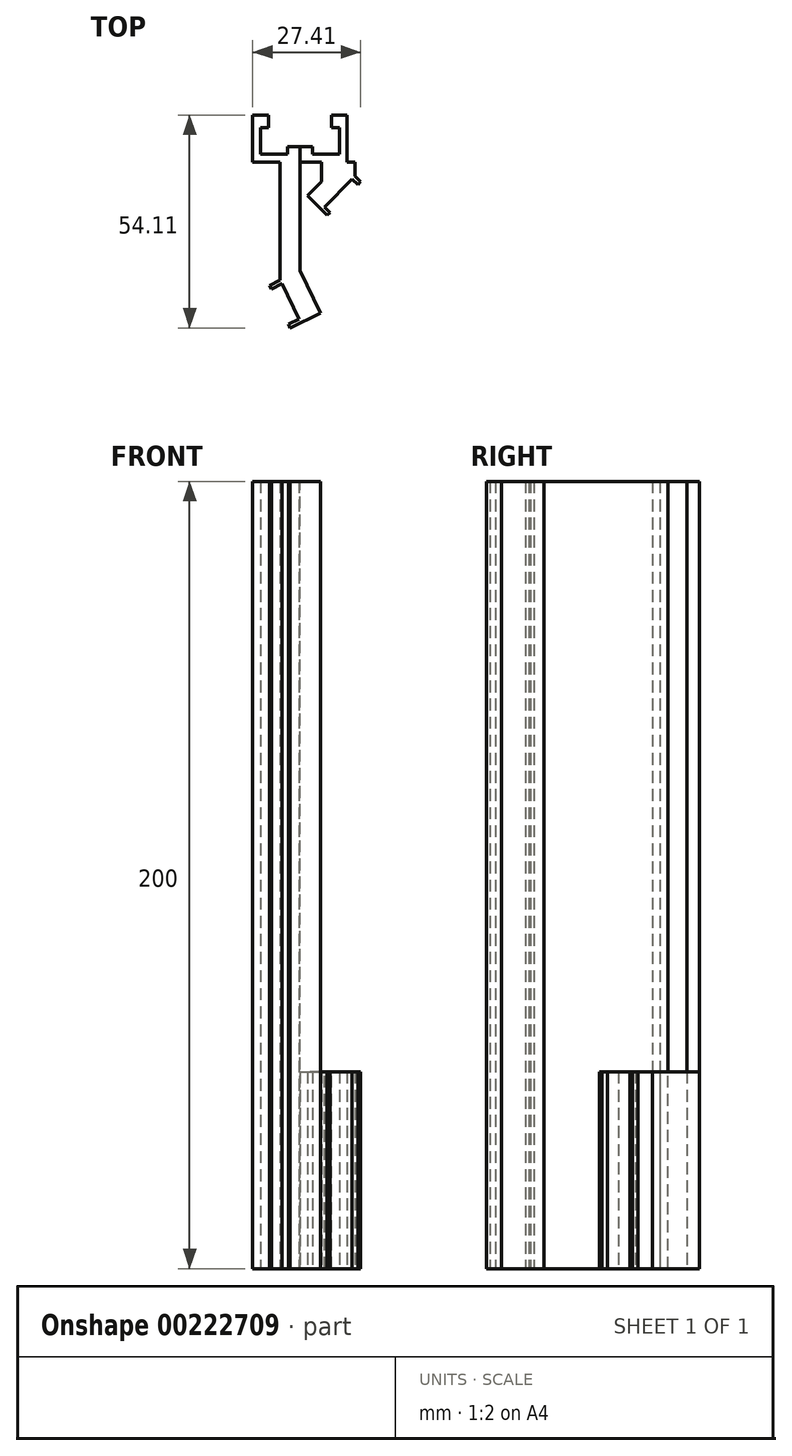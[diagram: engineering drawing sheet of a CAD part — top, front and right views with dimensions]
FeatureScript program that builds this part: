
annotation { "Feature Type Name" : "Feature", "Feature Type Description" : "" }
export const myFeature = defineFeature(function(context is Context, id is Id, definition is map)
    precondition{}
    {
        {
            var Q0;
            Q0=qCreatedBy(makeId("Top.planeOp"),FACE);
            var sketch = newSketch(context, id + "F0", { "sketchPlane" : qUnion([Q0])});
            skLineSegment(sketch, "E0", {"start": v(-10, 3) * mm, "end": v(-10, 10) * mm});
            skLineSegment(sketch, "E1", {"start": v(-10, 10) * mm, "end": v(-3, 10) * mm});
            skLineSegment(sketch, "E2", {"start": v(-3, 10) * mm, "end": v(-3, 8) * mm});
            skLineSegment(sketch, "E3", {"start": v(-3, 8) * mm, "end": v(3, 8) * mm});
            skLineSegment(sketch, "E4", {"start": v(3, 8) * mm, "end": v(3, 10) * mm});
            skLineSegment(sketch, "E5", {"start": v(3, 10) * mm, "end": v(10, 10) * mm});
            skLineSegment(sketch, "E6", {"start": v(10, 10) * mm, "end": v(10, 3) * mm});
            skLineSegment(sketch, "E7", {"start": v(10, 3) * mm, "end": v(8, 3) * mm});
            skLineSegment(sketch, "E8", {"start": v(8, 3) * mm, "end": v(8, -3) * mm});
            skLineSegment(sketch, "E9", {"start": v(8, -3) * mm, "end": v(10, -3) * mm});
            skLineSegment(sketch, "E10", {"start": v(10, -3) * mm, "end": v(10, -10) * mm});
            skLineSegment(sketch, "E11", {"start": v(10, -10) * mm, "end": v(3, -10) * mm});
            skLineSegment(sketch, "E12", {"start": v(3, -10) * mm, "end": v(3, -8) * mm});
            skLineSegment(sketch, "E13", {"start": v(3, -8) * mm, "end": v(-3, -8) * mm});
            skLineSegment(sketch, "E14", {"start": v(-3, -8) * mm, "end": v(-3, -10) * mm});
            skLineSegment(sketch, "E15", {"start": v(-3, -10) * mm, "end": v(-10, -10) * mm});
            skLineSegment(sketch, "E16", {"start": v(-10, -10) * mm, "end": v(-10, -3) * mm});
            skLineSegment(sketch, "E17", {"start": v(-10, -3) * mm, "end": v(-8, -3) * mm});
            skLineSegment(sketch, "E18", {"start": v(-8, -3) * mm, "end": v(-8, 3) * mm});
            skLineSegment(sketch, "E19", {"start": v(-8, 3) * mm, "end": v(-10, 3) * mm});
            skSolve(sketch);
        }
        {
            var Q0;
            Q0=qCreatedBy(makeId("Top.planeOp"),FACE);
            var sketch = newSketch(context, id + "F1", { "sketchPlane" : qUnion([Q0])});
            skLineSegment(sketch, "E20", {"start": v(0, 0) * mm, "end": v(-12, 0) * mm});
            skLineSegment(sketch, "E21", {"start": v(-12, 0) * mm, "end": v(-12, -12) * mm});
            skLineSegment(sketch, "E22", {"start": v(-12, -12) * mm, "end": v(-5, -12) * mm});
            skLineSegment(sketch, "E23", {"start": v(-5, -12) * mm, "end": v(-5, -42) * mm});
            skLineSegment(sketch, "E24", {"start": v(-5, -42) * mm, "end": v(0.24, -52.8) * mm});
            skLineSegment(sketch, "E25", {"start": v(0.24, -52.8) * mm, "end": v(5.24, -50.37) * mm});
            skLineSegment(sketch, "E26", {"start": v(5.24, -50.37) * mm, "end": v(0, -39.57) * mm});
            skLineSegment(sketch, "E27", {"start": v(0, -39.57) * mm, "end": v(0, 0) * mm});
            skLineSegment(sketch, "E28", {"start": v(-5, -42) * mm, "end": v(0, -39.57) * mm, "construction": true});
            skSolve(sketch);
        }
        {
            var Q0;
            Q0=makeQuery(id+"F1.imprint","IMPRINT",FACE,{"disambiguationData":[TD([[makeQuery(id+"F1.imprint","IMPRINT",EDGE,{"derivedFrom":sQuery(id+"F1.wireOp",EDGE,"E20")}),1.0]])]});
            extrude(context, id + "F2", {"entities" : qUnion([Q0]), "depth" : 200 * mm});
        }
        {
            var Q0;
            Q0=makeQuery(id+"F0.imprint","IMPRINT",FACE,{"disambiguationData":[TD([[makeQuery(id+"F0.imprint","IMPRINT",EDGE,{"derivedFrom":sQuery(id+"F0.wireOp",EDGE,"E0")}),-1.0]])]});
            extrude(context, id + "F3", {"entities" : qUnion([Q0]), "operationType" : NewBodyOperationType.REMOVE, "endBound" : BoundingType.THROUGH_ALL, "depth" : 25 * mm});
        }
        {
            var Q0;
            Q0=makeQuery(id+"F2.opExtrude","SWEPT_FACE",FACE,{"disambiguationData":[OSD([sQuery(id+"F1.wireOp",EDGE,"E24")])]});
            var sketch = newSketch(context, id + "F4", { "sketchPlane" : qUnion([Q0])});
            skLineSegment(sketch, "E29.bottom", {"start": v(35.6, 200) * mm, "end": v(36.6, 200) * mm});
            skLineSegment(sketch, "E29.top", {"start": v(35.6, 0) * mm, "end": v(36.6, 0) * mm});
            skLineSegment(sketch, "E29.left", {"start": v(35.6, 200) * mm, "end": v(35.6, 0) * mm});
            skLineSegment(sketch, "E29.right", {"start": v(36.6, 200) * mm, "end": v(36.6, 0) * mm});
            skLineSegment(sketch, "E30.bottom", {"start": v(47.6, 200) * mm, "end": v(46.6, 200) * mm});
            skLineSegment(sketch, "E30.top", {"start": v(47.6, 0) * mm, "end": v(46.6, 0) * mm});
            skLineSegment(sketch, "E30.left", {"start": v(47.6, 200) * mm, "end": v(47.6, 0) * mm});
            skLineSegment(sketch, "E30.right", {"start": v(46.6, 200) * mm, "end": v(46.6, 0) * mm});
            skSolve(sketch);
        }
        {
            var Q0;
            Q0=makeQuery(id+"F4.imprint","IMPRINT",FACE,{"disambiguationData":[TD([[makeQuery(id+"F4.imprint","IMPRINT",EDGE,{"derivedFrom":sQuery(id+"F4.wireOp",EDGE,"E29.bottom")}),-1.0]])]});
            var Q1;
            Q1=makeQuery(id+"F4.imprint","IMPRINT",FACE,{"disambiguationData":[TD([[makeQuery(id+"F4.imprint","IMPRINT",EDGE,{"derivedFrom":sQuery(id+"F4.wireOp",EDGE,"E30.bottom")}),-1.0]])]});
            extrude(context, id + "F5", {"entities" : qUnion([Q0, Q1]), "operationType" : NewBodyOperationType.ADD, "depth" : 3 * mm});
        }
        {
            var Q0;
            Q0=qCreatedBy(makeId("Top.planeOp"),FACE);
            var sketch = newSketch(context, id + "F6", { "sketchPlane" : qUnion([Q0])});
            skLineSegment(sketch, "E31", {"start": v(0, 0) * mm, "end": v(0, -12) * mm});
            skLineSegment(sketch, "E32", {"start": v(0, -12) * mm, "end": v(5.51, -12) * mm});
            skLineSegment(sketch, "E33", {"start": v(5.51, -12) * mm, "end": v(5.51, -17) * mm});
            skLineSegment(sketch, "E34", {"start": v(5.51, -17) * mm, "end": v(1.98, -20.54) * mm});
            skLineSegment(sketch, "E35", {"start": v(1.98, -20.54) * mm, "end": v(5.51, -24.07) * mm});
            skLineSegment(sketch, "E36", {"start": v(5.51, -24.07) * mm, "end": v(14, -15.59) * mm});
            skLineSegment(sketch, "E37", {"start": v(14, -15.59) * mm, "end": v(14, -12) * mm});
            skLineSegment(sketch, "E38", {"start": v(14, -12) * mm, "end": v(12, -12) * mm});
            skLineSegment(sketch, "E39", {"start": v(12, -12) * mm, "end": v(12, 0) * mm});
            skLineSegment(sketch, "E40", {"start": v(12, 0) * mm, "end": v(0, 0) * mm});
            skSolve(sketch);
        }
        {
            var Q0;
            Q0=makeQuery(id+"F6.imprint","IMPRINT",FACE,{"disambiguationData":[TD([[makeQuery(id+"F6.imprint","IMPRINT",EDGE,{"derivedFrom":sQuery(id+"F6.wireOp",EDGE,"E31")}),1.0]])]});
            extrude(context, id + "F7", {"entities" : qUnion([Q0]), "depth" : 50 * mm});
        }
        {
            var Q0;
            Q0=makeQuery(id+"F0.imprint","IMPRINT",FACE,{"disambiguationData":[TD([[makeQuery(id+"F0.imprint","IMPRINT",EDGE,{"derivedFrom":sQuery(id+"F0.wireOp",EDGE,"E0")}),-1.0]])]});
            extrude(context, id + "F8", {"entities" : qUnion([Q0]), "operationType" : NewBodyOperationType.REMOVE, "endBound" : BoundingType.THROUGH_ALL, "depth" : 25 * mm});
        }
        {
            var Q0;
            Q0=makeQuery(id+"F7.opExtrude","SWEPT_FACE",FACE,{"disambiguationData":[OSD([sQuery(id+"F6.wireOp",EDGE,"E36")])]});
            var sketch = newSketch(context, id + "F9", { "sketchPlane" : qUnion([Q0])});
            skLineSegment(sketch, "E41.bottom", {"start": v(-1.12, 50) * mm, "end": v(-2.12, 50) * mm});
            skLineSegment(sketch, "E41.top", {"start": v(-1.12, 0) * mm, "end": v(-2.12, 0) * mm});
            skLineSegment(sketch, "E41.left", {"start": v(-1.12, 50) * mm, "end": v(-1.12, 0) * mm});
            skLineSegment(sketch, "E41.right", {"start": v(-2.12, 50) * mm, "end": v(-2.12, 0) * mm});
            skLineSegment(sketch, "E42.bottom", {"start": v(-13.12, 0) * mm, "end": v(-12.12, 0) * mm});
            skLineSegment(sketch, "E42.top", {"start": v(-13.12, 50) * mm, "end": v(-12.12, 50) * mm});
            skLineSegment(sketch, "E42.left", {"start": v(-13.12, 0) * mm, "end": v(-13.12, 50) * mm});
            skLineSegment(sketch, "E42.right", {"start": v(-12.12, 0) * mm, "end": v(-12.12, 50) * mm});
            skSolve(sketch);
        }
        {
            var Q0;
            Q0=makeQuery(id+"F9.imprint","IMPRINT",FACE,{"disambiguationData":[TD([[makeQuery(id+"F9.imprint","IMPRINT",EDGE,{"derivedFrom":sQuery(id+"F9.wireOp",EDGE,"E42.bottom")}),1.0]])]});
            var Q1;
            Q1=makeQuery(id+"F9.imprint","IMPRINT",FACE,{"disambiguationData":[TD([[makeQuery(id+"F9.imprint","IMPRINT",EDGE,{"derivedFrom":sQuery(id+"F9.wireOp",EDGE,"E41.bottom")}),-1.0]])]});
            extrude(context, id + "F10", {"entities" : qUnion([Q0, Q1]), "operationType" : NewBodyOperationType.ADD, "depth" : 2 * mm});
        }
        {
            var Q0;
            Q0=makeQuery(id+"F3.boolean.opBoolean","COPY",FACE,{"derivedFrom":makeQuery(id+"F3.opExtrude","SWEPT_FACE",FACE,{"disambiguationData":[OSD([sQuery(id+"F0.wireOp",EDGE,"E17")])]})});
            var Q1;
            Q1=makeQuery(id+"F8.boolean.opBoolean","COPY",FACE,{"derivedFrom":makeQuery(id+"F8.opExtrude","SWEPT_FACE",FACE,{"disambiguationData":[OSD([sQuery(id+"F0.wireOp",EDGE,"E9")])]})});
            extrude(context, id + "F11", {"entities" : qUnion([Q0, Q1]), "operationType" : NewBodyOperationType.ADD, "depth" : .2 * mm});
        }
        {
            var Q0;
            Q0=makeQuery(id+"F8.boolean.opBoolean","COPY",FACE,{"derivedFrom":makeQuery(id+"F8.opExtrude","SWEPT_FACE",FACE,{"disambiguationData":[OSD([sQuery(id+"F0.wireOp",EDGE,"E12")])]})});
            extrude(context, id + "F12", {"entities" : qUnion([Q0]), "operationType" : NewBodyOperationType.ADD, "depth" : .2 * mm});
        }
        {
            var Q0;
            Q0=makeQuery(id+"F3.boolean.opBoolean","COPY",FACE,{"derivedFrom":makeQuery(id+"F3.opExtrude","SWEPT_FACE",FACE,{"disambiguationData":[OSD([sQuery(id+"F0.wireOp",EDGE,"E14")])]})});
            extrude(context, id + "F13", {"entities" : qUnion([Q0]), "operationType" : NewBodyOperationType.ADD, "depth" : .2 * mm});
        }
    });
